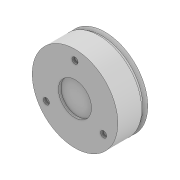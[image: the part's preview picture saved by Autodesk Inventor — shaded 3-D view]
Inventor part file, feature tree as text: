
AUTODESK INVENTOR PART (.ipt)
format: ipt  version: 2020 (Build 240168000, 168)  size: 127,488 bytes
history: native  units: mm
features: other x5, sketch x5, extrude x3, loft x2, projected_geometry x1
ambient origin geometry x8: Origin, YZ Plane, XZ Plane, XY Plane, X Axis, Y Axis, Z Axis, Center Point
bodies: Body1 (feature_tree)
feature tree (16):
  other  "솔리드1"
  extrude  "돌출1"  Depth=70.0mm
  extrude  "돌출2"  Depth=19.5mm TaperAngle=0.0deg
  other  "작업 평면1"
  loft  "로프트1"
  other  "작업 평면2"
  loft  "로프트2"
  extrude  "돌출3"  Depth=30.0mm TaperAngle=360.0deg
  sketch  "스케치1"
  sketch  "스케치2"
  projected_geometry  "투영된 루프1"
  sketch  "스케치4"
  other  "모서리1"
  sketch  "스케치5"
  other  "모서리2"
  sketch  "스케치6"
